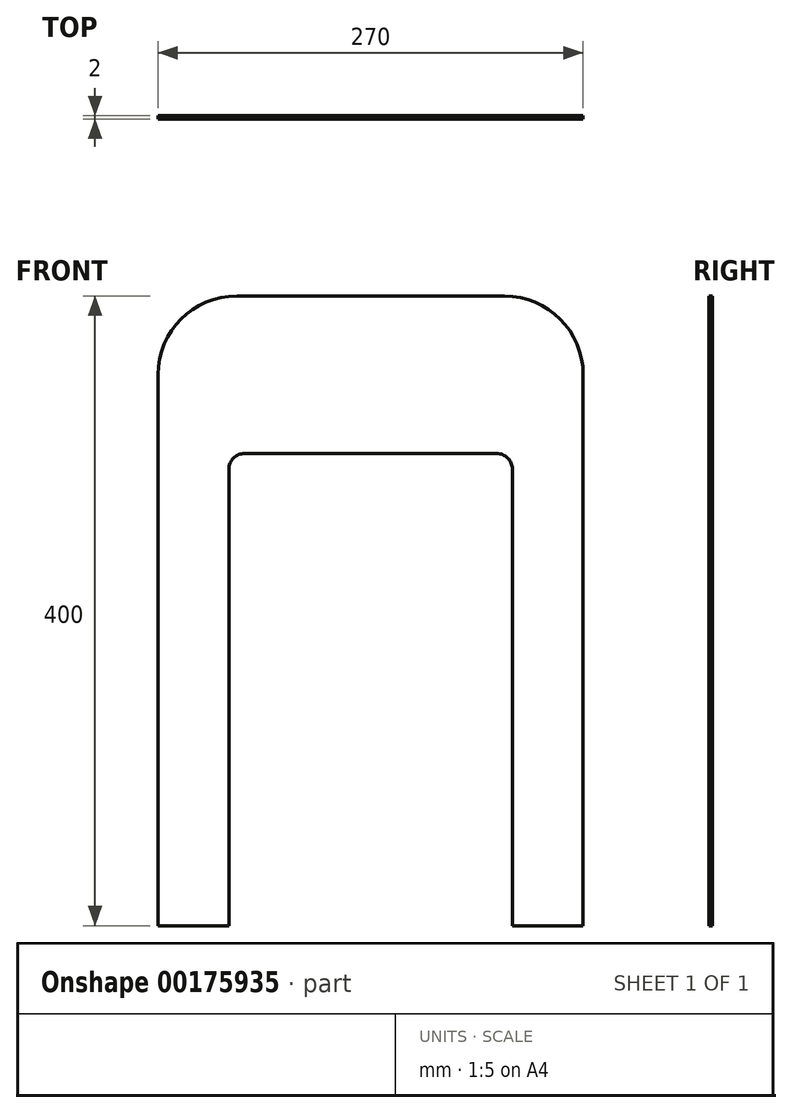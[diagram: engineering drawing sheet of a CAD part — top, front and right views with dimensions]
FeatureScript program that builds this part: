
annotation { "Feature Type Name" : "Feature", "Feature Type Description" : "" }
export const myFeature = defineFeature(function(context is Context, id is Id, definition is map)
    precondition{}
    {
        {
            var Q0;
            Q0=qCreatedBy(makeId("Front.planeOp"),FACE);
            var sketch = newSketch(context, id + "F0", { "sketchPlane" : qUnion([Q0])});
            skLineSegment(sketch, "E0", {"start": v(0, 0) * mm, "end": v(-85, 0) * mm});
            skLineSegment(sketch, "E1", {"start": v(-135, -50) * mm, "end": v(-135, -400) * mm});
            skLineSegment(sketch, "E2", {"start": v(-135, -400) * mm, "end": v(-90, -400) * mm});
            skLineSegment(sketch, "E3", {"start": v(-90, -400) * mm, "end": v(-90, -110) * mm});
            skLineSegment(sketch, "E4", {"start": v(-80, -100) * mm, "end": v(0, -100) * mm});
            skPoint(sketch, "E5.visualSharp", {"position": v(-135, 0) * mm});
            skArc(sketch, "E5.filletArc", {"start": v(-85, 0) * mm, "mid": v(-120.36, -14.64) * mm, "end": v(-135, -50) * mm});
            skPoint(sketch, "E6.visualSharp", {"position": v(-90, -100) * mm});
            skArc(sketch, "E6.filletArc", {"start": v(-80, -100) * mm, "mid": v(-87.07, -102.93) * mm, "end": v(-90, -110) * mm});
            skArc(sketch, "E7.MirrorCS", {"start": v(80, -100) * mm, "mid": v(87.07, -102.93) * mm, "end": v(90, -110) * mm});
            skLineSegment(sketch, "E8.MirrorCS", {"start": v(0, 0) * mm, "end": v(85, 0) * mm});
            skLineSegment(sketch, "E9.MirrorCS", {"start": v(135, -50) * mm, "end": v(135, -400) * mm});
            skLineSegment(sketch, "E10.MirrorCS", {"start": v(135, -400) * mm, "end": v(90, -400) * mm});
            skLineSegment(sketch, "E11.MirrorCS", {"start": v(90, -400) * mm, "end": v(90, -110) * mm});
            skPoint(sketch, "E12.MirrorP", {"position": v(135, 0) * mm});
            skLineSegment(sketch, "E13.MirrorCS", {"start": v(80, -100) * mm, "end": v(0, -100) * mm});
            skArc(sketch, "E14.MirrorCS", {"start": v(85, 0) * mm, "mid": v(120.36, -14.64) * mm, "end": v(135, -50) * mm});
            skPoint(sketch, "E15.MirrorP", {"position": v(90, -100) * mm});
            skSolve(sketch);
        }
        {
            var Q0;
            Q0=makeQuery(id+"F0.imprint","IMPRINT",FACE,{"disambiguationData":[TD([[makeQuery(id+"F0.imprint","IMPRINT",EDGE,{"derivedFrom":sQuery(id+"F0.wireOp",EDGE,"E0")}),1.0]])]});
            extrude(context, id + "F1", {"entities" : qUnion([Q0]), "depth" : 2 * mm});
        }
    });
